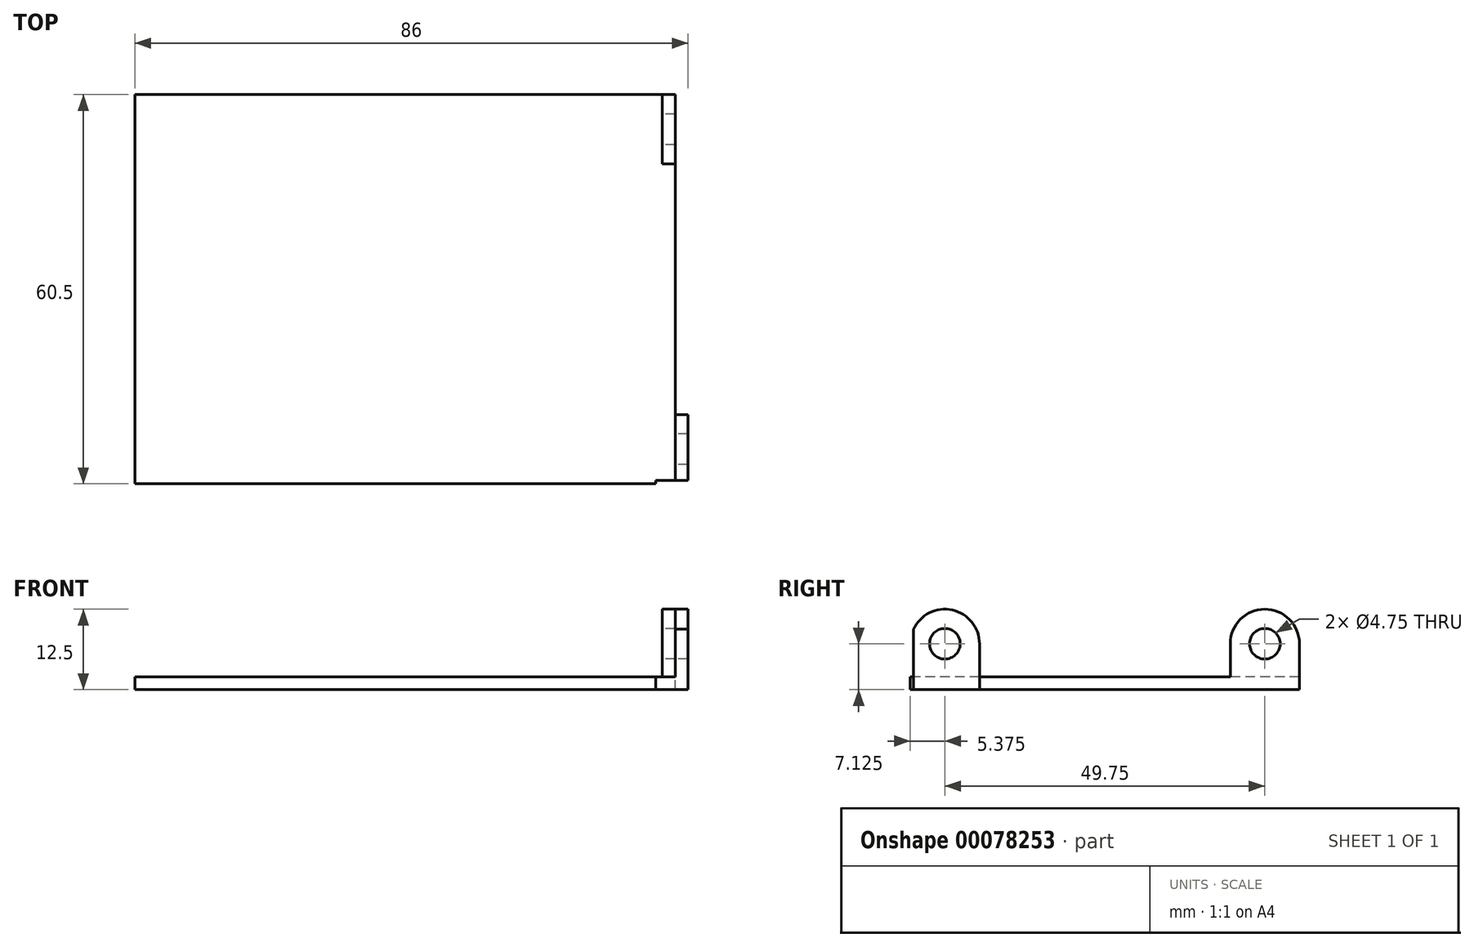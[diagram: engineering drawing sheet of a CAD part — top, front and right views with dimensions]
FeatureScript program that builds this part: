
annotation { "Feature Type Name" : "Feature", "Feature Type Description" : "" }
export const myFeature = defineFeature(function(context is Context, id is Id, definition is map)
    precondition{}
    {
        {
            var Q0;
            Q0=qCreatedBy(makeId("Top.planeOp"),FACE);
            var sketch = newSketch(context, id + "F0", { "sketchPlane" : qUnion([Q0])});
            skLineSegment(sketch, "E0.bottom", {"start": v(41, 30.25) * mm, "end": v(-41, 30.25) * mm});
            skLineSegment(sketch, "E0.top", {"start": v(41, -30.25) * mm, "end": v(-41, -30.25) * mm});
            skLineSegment(sketch, "E0.left", {"start": v(41, 30.25) * mm, "end": v(41, -30.25) * mm});
            skLineSegment(sketch, "E0.right", {"start": v(-41, 30.25) * mm, "end": v(-41, -30.25) * mm});
            skPoint(sketch, "E0.middle", {"position": v(0, 0) * mm});
            skSolve(sketch);
        }
        {
            var Q0;
            Q0 = qSketchRegion(id + "F0", true);
            extrude(context, id + "F1", {"entities" : qUnion([Q0]), "depth" : 2 * mm});
        }
        {
            var Q0;
            Q0=makeQuery(id+"F1.opExtrude","SWEPT_FACE",FACE,{"disambiguationData":[OSD([sQuery(id+"F0.wireOp",EDGE,"E0.left")])]});
            var sketch = newSketch(context, id + "F2", { "sketchPlane" : qUnion([Q0])});
            skLineSegment(sketch, "E1.bottom", {"start": v(-19.5, 2) * mm, "end": v(19.5, 2) * mm});
            skLineSegment(sketch, "E1.top", {"start": v(-30.25, 0) * mm, "end": v(-30.25, 0) * mm});
            skLineSegment(sketch, "E1.left", {"start": v(-30.25, 2) * mm, "end": v(-30.25, 0) * mm});
            skLineSegment(sketch, "E1.right", {"start": v(30.25, 2) * mm, "end": v(30.25, 0) * mm});
            skLineSegment(sketch, "E2.trimOffspring", {"start": v(30.25, 0) * mm, "end": v(30.25, 0) * mm});
            skLineSegment(sketch, "E3", {"start": v(-30.25, 1) * mm, "end": v(30.25, 1) * mm, "construction": true});
            skLineSegment(sketch, "E4.MirrorCS", {"start": v(-30.25, 7.12) * mm, "end": v(-30.25, 2) * mm});
            skArc(sketch, "E5.MirrorCS", {"start": v(-30.25, 7.12) * mm, "mid": v(-24.87, 12.5) * mm, "end": v(-19.5, 7.12) * mm});
            skCircle(sketch, "E6.MirrorC", {"center": v(-24.87, 7.12) * mm, "radius": 2.38 * mm});
            skLineSegment(sketch, "E7.MirrorCS", {"start": v(-19.5, 7.12) * mm, "end": v(-19.5, 2) * mm});
            skLineSegment(sketch, "E8.MirrorCS", {"start": v(0, 2) * mm, "end": v(0, 7.12) * mm, "construction": true});
            skLineSegment(sketch, "E9.MirrorCS", {"start": v(-24.87, 7.12) * mm, "end": v(24.87, 7.12) * mm, "construction": true});
            skLineSegment(sketch, "E10.MirrorCS", {"start": v(19.5, 7.12) * mm, "end": v(19.5, 2) * mm});
            skArc(sketch, "E11.MirrorCS", {"start": v(30.25, 7.12) * mm, "mid": v(24.87, 12.5) * mm, "end": v(19.5, 7.12) * mm});
            skCircle(sketch, "E12.MirrorC", {"center": v(24.87, 7.12) * mm, "radius": 2.38 * mm});
            skLineSegment(sketch, "E13.MirrorCS", {"start": v(30.25, 7.12) * mm, "end": v(30.25, 2) * mm});
            skLineSegment(sketch, "E14", {"start": v(-30.25, 0) * mm, "end": v(30.25, 0) * mm});
            skSolve(sketch);
        }
        {
            var Q0;
            {var subQ2=sQuery(id+"F2.wireOp",EDGE,"E1.bottom");Q0=makeQuery(id+"F2.imprint","IMPRINT",FACE,{"disambiguationData":[TD([[makeQuery(id+"F2.imprint","IMPRINT",EDGE,{"derivedFrom":subQ2}),1.0]])]});}
            var Q1;
            {var subQ1=sQuery(id+"F2.wireOp",EDGE,"E10.MirrorCS");Q1=makeQuery(id+"F2.imprint","IMPRINT",FACE,{"disambiguationData":[TD([[makeQuery(id+"F2.imprint","IMPRINT",EDGE,{"derivedFrom":subQ1}),1.0]])]});}
            extrude(context, id + "F3", {"entities" : qUnion([Q0, Q1]), "operationType" : NewBodyOperationType.ADD, "depth" : 2 * mm});
        }
        {
            var Q0;
            {var subQ1=sQuery(id+"F2.wireOp",EDGE,"E4.MirrorCS");Q0=makeQuery(id+"F2.imprint","IMPRINT",FACE,{"disambiguationData":[TD([[makeQuery(id+"F2.imprint","IMPRINT",EDGE,{"derivedFrom":subQ1}),1.0]])]});}
            extrude(context, id + "F4", {"entities" : qUnion([Q0]), "operationType" : NewBodyOperationType.ADD, "depth" : 4 * mm});
        }
        {
            var Q0;
            Q0=makeQuery(id+"F4.opExtrude","SWEPT_FACE",FACE,{"disambiguationData":[OSD([sQuery(id+"F0.wireOp",EDGE,"E0.left")])]});
            extrude(context, id + "F5", {"entities" : qUnion([Q0]), "operationType" : NewBodyOperationType.ADD, "depth" : 2 * mm});
        }
        {
            var Q0;
            {var subQ0=sQuery(id+"F0.wireOp",EDGE,"E0.left");Q0=makeQuery(id+"F3.boolean.opBoolean","MERGE",FACE,{"derivedFrom":[makeQuery(id+"F1.opExtrude","CAP_FACE",FACE,{"disambiguationData":[OSD([sQuery(id+"F0.wireOp",EDGE,"E0.bottom"),sQuery(id+"F0.wireOp",EDGE,"E0.top"),subQ0,sQuery(id+"F0.wireOp",EDGE,"E0.right")])],"isStart":true}),makeQuery(id+"F3.opExtrude","SWEPT_FACE",FACE,{"disambiguationData":[OSD([sQuery(id+"F2.wireOp",EDGE,"E1.top")])]}),makeQuery(id+"F3.opExtrude","SWEPT_FACE",FACE,{"disambiguationData":[OSD([subQ0,sQuery(id+"F2.wireOp",EDGE,"c8340855-5e98-4a63-a587-fe606d19c6f9.trimOffspring"),sQuery(id+"F2.wireOp",EDGE,"E2.trimOffspring")])]})]});}
            var sketch = newSketch(context, id + "F6", { "sketchPlane" : qUnion([Q0])});
            skLineSegment(sketch, "E15", {"start": v(41, -19.5) * mm, "end": v(41, -30.25) * mm});
            skLineSegment(sketch, "E16", {"start": v(41, -30.25) * mm, "end": v(43, -30.25) * mm});
            skLineSegment(sketch, "E17", {"start": v(41, -19.5) * mm, "end": v(43, -19.5) * mm});
            skLineSegment(sketch, "E18", {"start": v(43, -19.5) * mm, "end": v(43, -30.25) * mm});
            skSolve(sketch);
        }
        {
            var Q0;
            Q0 = qSketchRegion(id + "F6", true);
            extrude(context, id + "F7", {"entities" : qUnion([Q0]), "operationType" : NewBodyOperationType.REMOVE, "endBound" : BoundingType.THROUGH_ALL, "depth" : 25 * mm});
        }
        {
            var Q0;
            {var subQ0=sQuery(id+"F0.wireOp",EDGE,"E0.left");Q0=makeQuery(id+"F5.boolean.opBoolean","MERGE",FACE,{"derivedFrom":[makeQuery(id+"F4.opExtrude","CAP_FACE",FACE,{"disambiguationData":[OSD([subQ0,sQuery(id+"F2.wireOp",EDGE,"E4.MirrorCS"),sQuery(id+"F2.wireOp",EDGE,"E5.MirrorCS"),sQuery(id+"F2.wireOp",EDGE,"E6.MirrorC"),sQuery(id+"F2.wireOp",EDGE,"E7.MirrorCS")])],"isStart":false}),makeQuery(id+"F5.opExtrude","SWEPT_FACE",FACE,{"disambiguationData":[OSD([subQ0])]})]});}
            var sketch = newSketch(context, id + "F8", { "sketchPlane" : qUnion([Q0])});
            skLineSegment(sketch, "E19.bottom", {"start": v(-30.25, 0) * mm, "end": v(-29.75, 0) * mm});
            skLineSegment(sketch, "E19.top", {"start": v(-30.25, 10) * mm, "end": v(-29.75, 10) * mm});
            skLineSegment(sketch, "E19.left", {"start": v(-30.25, 0) * mm, "end": v(-30.25, 10) * mm});
            skLineSegment(sketch, "E19.right", {"start": v(-29.75, 0) * mm, "end": v(-29.75, 10) * mm});
            skSolve(sketch);
        }
        {
            var Q0;
            Q0 = qSketchRegion(id + "F8", true);
            extrude(context, id + "F9", {"entities" : qUnion([Q0]), "operationType" : NewBodyOperationType.REMOVE, "oppositeDirection" : true, "depth" : 5 * mm});
        }
    });
